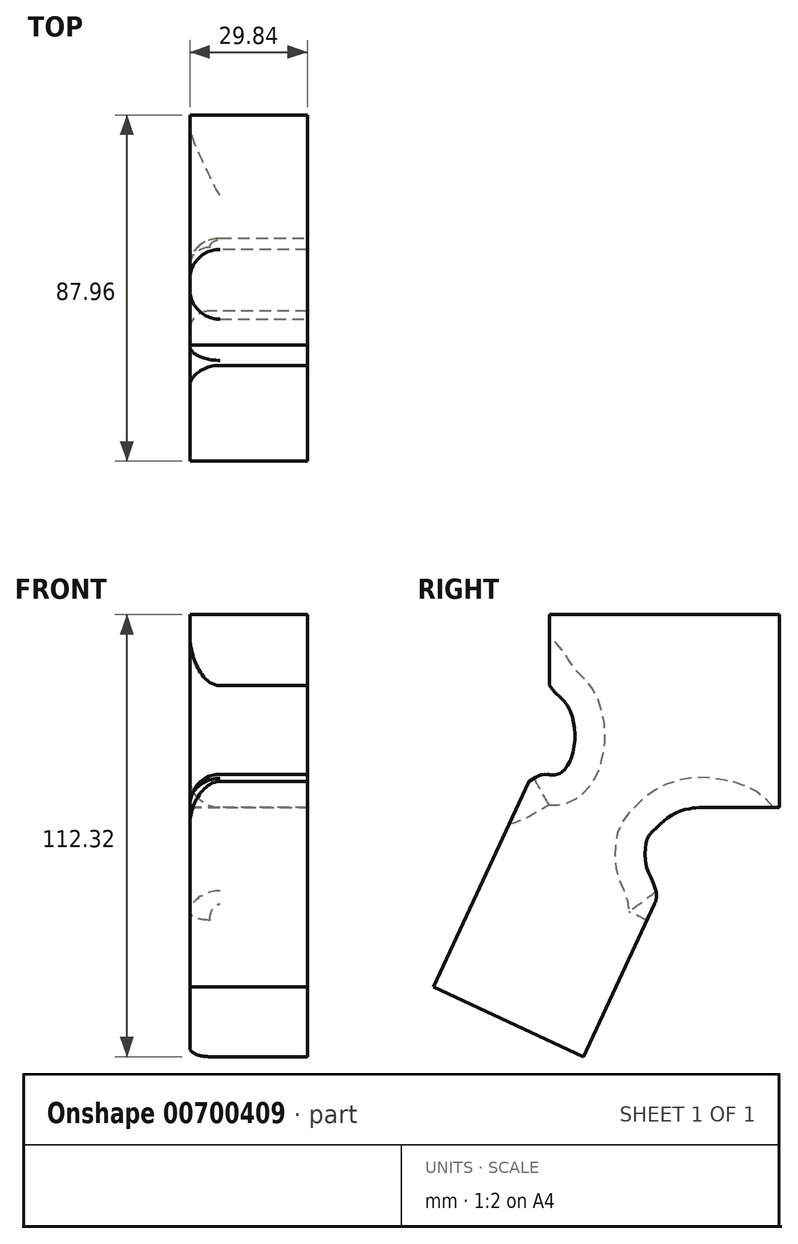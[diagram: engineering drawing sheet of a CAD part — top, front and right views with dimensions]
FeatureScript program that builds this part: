
annotation { "Feature Type Name" : "Feature", "Feature Type Description" : "" }
export const myFeature = defineFeature(function(context is Context, id is Id, definition is map)
    precondition{}
    {
        {
            var Q0;
            Q0=qCreatedBy(makeId("Front.planeOp"),FACE);
            var sketch = newSketch(context, id + "F0", { "sketchPlane" : qUnion([Q0])});
            skLineSegment(sketch, "E0.bottom", {"start": v(18.21, 19.14) * mm, "end": v(10, 19.14) * mm, "construction": true});
            skLineSegment(sketch, "E0.top", {"start": v(13.9, -19.14) * mm, "end": v(-13.9, -19.14) * mm, "construction": true});
            skLineSegment(sketch, "E0.left", {"start": v(20.24, 17.1) * mm, "end": v(20.24, -12.79) * mm, "construction": true});
            skLineSegment(sketch, "E0.right", {"start": v(-20.24, 17.1) * mm, "end": v(-20.24, -12.79) * mm, "construction": true});
            skPoint(sketch, "E0.middle", {"position": v(0, 0) * mm});
            skLineSegment(sketch, "E1", {"start": v(-10, 19.14) * mm, "end": v(-18.21, 19.14) * mm, "construction": true});
            skPoint(sketch, "E2.visualSharp", {"position": v(-20.24, -19.14) * mm});
            skArc(sketch, "E2.filletArc", {"start": v(-20.24, -12.79) * mm, "mid": v(-18.38, -17.28) * mm, "end": v(-13.9, -19.14) * mm, "construction": true});
            skPoint(sketch, "E3.visualSharp", {"position": v(20.24, -19.14) * mm});
            skArc(sketch, "E3.filletArc", {"start": v(13.9, -19.14) * mm, "mid": v(18.38, -17.28) * mm, "end": v(20.24, -12.79) * mm, "construction": true});
            skPoint(sketch, "E4.visualSharp", {"position": v(20.24, 19.14) * mm});
            skArc(sketch, "E4.filletArc", {"start": v(20.24, 17.1) * mm, "mid": v(19.65, 18.54) * mm, "end": v(18.21, 19.14) * mm, "construction": true});
            skPoint(sketch, "E5.visualSharp", {"position": v(-20.24, 19.14) * mm});
            skArc(sketch, "E5.filletArc", {"start": v(-18.21, 19.14) * mm, "mid": v(-19.65, 18.54) * mm, "end": v(-20.24, 17.1) * mm, "construction": true});
            skArc(sketch, "E6", {"start": v(-10, 19.14) * mm, "mid": v(-8.4, 15.2) * mm, "end": v(-5.33, 12.27) * mm, "construction": true});
            skArc(sketch, "E7", {"start": v(-5.33, -2.2) * mm, "mid": v(0, -7.53) * mm, "end": v(5.33, -2.2) * mm, "construction": true});
            skLineSegment(sketch, "E8", {"start": v(-5.33, -2.2) * mm, "end": v(-5.33, 12.27) * mm, "construction": true});
            skLineSegment(sketch, "E9", {"start": v(5.33, -2.2) * mm, "end": v(5.33, 12.27) * mm, "construction": true});
            skPoint(sketch, "E10.orphan", {"position": v(0, 19.14) * mm});
            skArc(sketch, "E11.trimOffspring", {"start": v(5.33, 12.27) * mm, "mid": v(8.4, 15.2) * mm, "end": v(10, 19.14) * mm, "construction": true});
            skSolve(sketch);
        }
        {
            var Q0;
            Q0=qCreatedBy(makeId("Front.planeOp"),FACE);
            var sketch = newSketch(context, id + "F1", { "sketchPlane" : qUnion([Q0])});
            skLineSegment(sketch, "E12.bottom", {"start": v(-14.92, -49.02) * mm, "end": v(14.92, -49.02) * mm});
            skLineSegment(sketch, "E12.top", {"start": v(-14.92, 0) * mm, "end": v(14.92, 0) * mm});
            skLineSegment(sketch, "E12.left", {"start": v(-14.92, -49.02) * mm, "end": v(-14.92, 0) * mm});
            skLineSegment(sketch, "E12.right", {"start": v(14.92, -49.02) * mm, "end": v(14.92, 0) * mm});
            skSolve(sketch);
        }
        {
            var Q0;
            Q0=makeQuery(id+"F1.imprint","IMPRINT",FACE,{"disambiguationData":[TD([[makeQuery(id+"F1.imprint","IMPRINT",EDGE,{"derivedFrom":sQuery(id+"F1.wireOp",EDGE,"E12.bottom")}),1.0]])]});
            extrude(context, id + "F2", {"entities" : qUnion([Q0]), "oppositeDirection" : true, "depth" : 58.42 * mm, "offsetDistance" : 25.4 * mm});
        }
        {
            var Q0;
            Q0=makeQuery(id+"F2.opExtrude","SWEPT_FACE",FACE,{"disambiguationData":[OSD([sQuery(id+"F1.wireOp",EDGE,"E12.left")])]});
            var sketch = newSketch(context, id + "F3", { "sketchPlane" : qUnion([Q0])});
            skPoint(sketch, "E13", {"position": v(0, -31.24) * mm});
            skPoint(sketch, "E14", {"position": v(-38.1, -49.02) * mm});
            skSolve(sketch);
        }
        {
            var Q0;
            Q0=makeQuery(id+"F2.opExtrude","CAP_FACE",FACE,{"disambiguationData":[OSD([sQuery(id+"F1.wireOp",EDGE,"E12.bottom"),sQuery(id+"F1.wireOp",EDGE,"E12.top"),sQuery(id+"F1.wireOp",EDGE,"E12.left"),sQuery(id+"F1.wireOp",EDGE,"E12.right")])],"isStart":true});
            var sketch = newSketch(context, id + "F4", { "sketchPlane" : qUnion([Q0])});
            skPoint(sketch, "E15", {"position": v(14.92, -31.24) * mm});
            skSolve(sketch);
        }
        {
            var Q0;
            Q0=sQuery(id+"F4.wireOp",VERTEX,"E15");
            var Q1;
            Q1=sQuery(id+"F3.wireOp",VERTEX,"E13");
            var Q2;
            Q2=sQuery(id+"F3.wireOp",VERTEX,"E14");
            cPlane(context, id + "F5", {"entities" : qUnion([Q0, Q1, Q2]), "cplaneType" : CPlaneType.THREE_POINT, "offset" : 25.4 * mm, "width" : 152.4 * mm, "height" : 152.4 * mm});
        }
        {
            var Q0;
            Q0=qCreatedBy(id+"F5.planeOp",FACE);
            var sketch = newSketch(context, id + "F6", { "sketchPlane" : qUnion([Q0])});
            skPoint(sketch, "E16", {"position": v(14.92, 55.26) * mm});
            skLineSegment(sketch, "E17.bottom", {"start": v(14.92, 55.26) * mm, "end": v(-14.92, 55.26) * mm});
            skLineSegment(sketch, "E17.top", {"start": v(14.92, 13.21) * mm, "end": v(-14.92, 13.21) * mm});
            skLineSegment(sketch, "E17.left", {"start": v(14.92, 55.26) * mm, "end": v(14.92, 13.21) * mm});
            skLineSegment(sketch, "E17.right", {"start": v(-14.92, 55.26) * mm, "end": v(-14.92, 13.21) * mm});
            skSolve(sketch);
        }
        {
            var Q0;
            Q0 = qSketchRegion(id + "F6", true);
            extrude(context, id + "F7", {"entities" : qUnion([Q0]), "operationType" : NewBodyOperationType.ADD, "oppositeDirection" : true, "depth" : 69.85 * mm, "offsetDistance" : 25.4 * mm});
        }
        {
            var Q0;
            Q0=makeQuery(id+"F7.boolean.opBoolean","MERGE",FACE,{"derivedFrom":[makeQuery(id+"F2.opExtrude","SWEPT_FACE",FACE,{"disambiguationData":[OSD([sQuery(id+"F1.wireOp",EDGE,"E12.right")])]}),makeQuery(id+"F7.opExtrude","SWEPT_FACE",FACE,{"disambiguationData":[OSD([sQuery(id+"F6.wireOp",EDGE,"E17.left")])]})]});
            var sketch = newSketch(context, id + "F8", { "sketchPlane" : qUnion([Q0])});
            skFitSpline(sketch, "E18", {"points": [v(0, -18.02) * mm, v(4.4, -22.8) * mm, v(5.94, -26.72) * mm, v(6.49, -30.91) * mm, v(5.7, -35.8) * mm, v(4.71, -38.16) * mm, v(2.07, -40.62) * mm, v(-1.25, -40.6) * mm, v(-5.2, -42.4) * mm, v(-16.06, -44.8) * mm, v(-7.34, -11.16) * mm, v(0, -18.02) * mm]});
            skFitSpline(sketch, "E19", {"points": [v(24.38, -58.89) * mm, v(25.2, -56.3) * mm, v(28.17, -53.19) * mm, v(30.73, -51.14) * mm, v(34, -49.66) * mm, v(36.42, -49.16) * mm, v(38.1, -49.02) * mm, v(48.86, -51.66) * mm, v(49.95, -63.07) * mm, v(30.52, -81.16) * mm, v(27.03, -70.23) * mm, v(24.64, -64.32) * mm, v(24.38, -58.89) * mm]});
            skPoint(sketch, "E20", {"position": v(27.36, -72.04) * mm});
            skSolve(sketch);
        }
        {
            var Q0;
            {var subQ0=sQuery(id+"F8.wireOp",EDGE,"E18");var subQ3=makeQuery(id+"F2.opExtrude","CAP_EDGE",EDGE,{"disambiguationData":[OSD([sQuery(id+"F1.wireOp",EDGE,"E12.right")])],"isStart":true});var subQ4=makeQuery(id+"F8.imprint","INTERSECT",VERTEX,{"derivedFrom":[subQ3,subQ0]});Q0=makeQuery(id+"F8.imprint","IMPRINT",FACE,{"disambiguationData":[TD([[makeQuery(id+"F8.imprint","IMPRINT",EDGE,{"disambiguationData":[TD([[subQ4,-1.0]])],"derivedFrom":subQ0}),-1.0]])]});}
            var Q1;
            {var subQ0=sQuery(id+"F8.wireOp",EDGE,"E19");var subQ1=makeQuery(id+"F7.opExtrude","SWEPT_EDGE",EDGE,{"disambiguationData":[OSD([sQuery(id+"F6.wireOp",EDGE,"E17.bottom"),sQuery(id+"F6.wireOp",EDGE,"E17.left")])]});var subQ3=makeQuery(id+"F8.imprint","INTERSECT",VERTEX,{"derivedFrom":[subQ1,subQ0]});Q1=makeQuery(id+"F8.imprint","IMPRINT",FACE,{"disambiguationData":[TD([[makeQuery(id+"F8.imprint","IMPRINT",EDGE,{"disambiguationData":[TD([[subQ3,-1.0]])],"derivedFrom":subQ0}),-1.0]])]});}
            extrude(context, id + "F9", {"entities" : qUnion([Q0, Q1]), "operationType" : NewBodyOperationType.REMOVE, "oppositeDirection" : true, "depth" : 34.3 * mm, "offsetDistance" : 25.4 * mm});
        }
        {
            var Q0;
            Q0=makeQuery(id+"F9.boolean.opBoolean","COPY",EDGE,{"derivedFrom":makeQuery(id+"F9.opExtrude","CAP_EDGE",EDGE,{"disambiguationData":[OSD([sQuery(id+"F8.wireOp",EDGE,"E19")])],"isStart":true})});
            var Q1;
            Q1=makeQuery(id+"F9.boolean.opBoolean","INTERSECT",EDGE,{"derivedFrom":[makeQuery(id+"F7.boolean.opBoolean","MERGE",FACE,{"derivedFrom":[makeQuery(id+"F2.opExtrude","SWEPT_FACE",FACE,{"disambiguationData":[OSD([sQuery(id+"F1.wireOp",EDGE,"E12.left")])]}),makeQuery(id+"F7.opExtrude","SWEPT_FACE",FACE,{"disambiguationData":[OSD([sQuery(id+"F6.wireOp",EDGE,"E17.right")])]})]}),makeQuery(id+"F9.opExtrude","SWEPT_FACE",FACE,{"disambiguationData":[OSD([sQuery(id+"F8.wireOp",EDGE,"E19")])]})]});
            var Q2;
            Q2=makeQuery(id+"F9.boolean.opBoolean","COPY",EDGE,{"derivedFrom":makeQuery(id+"F9.opExtrude","CAP_EDGE",EDGE,{"disambiguationData":[OSD([sQuery(id+"F8.wireOp",EDGE,"E18")])],"isStart":true})});
            var Q3;
            Q3=makeQuery(id+"F9.boolean.opBoolean","INTERSECT",EDGE,{"derivedFrom":[makeQuery(id+"F7.boolean.opBoolean","MERGE",FACE,{"derivedFrom":[makeQuery(id+"F2.opExtrude","SWEPT_FACE",FACE,{"disambiguationData":[OSD([sQuery(id+"F1.wireOp",EDGE,"E12.left")])]}),makeQuery(id+"F7.opExtrude","SWEPT_FACE",FACE,{"disambiguationData":[OSD([sQuery(id+"F6.wireOp",EDGE,"E17.right")])]})]}),makeQuery(id+"F9.opExtrude","SWEPT_FACE",FACE,{"disambiguationData":[OSD([sQuery(id+"F8.wireOp",EDGE,"E18")])]})]});
            fillet(context, id + "F10", {"entities" : qUnion([Q0, Q1, Q2, Q3]), "radius" : 7.62 * mm, "tangentPropagation" : true, "allowEdgeOverflow" : false});
        }
        {
            var Q0;
            Q0=makeQuery(id+"F7.opExtrude","SWEPT_EDGE",EDGE,{"disambiguationData":[OSD([sQuery(id+"F6.wireOp",EDGE,"E17.bottom"),sQuery(id+"F6.wireOp",EDGE,"E17.right")])]});
            fillet(context, id + "F11", {"entities" : qUnion([Q0]), "radius" : 5.08 * mm, "tangentPropagation" : true, "allowEdgeOverflow" : false});
        }
    });
